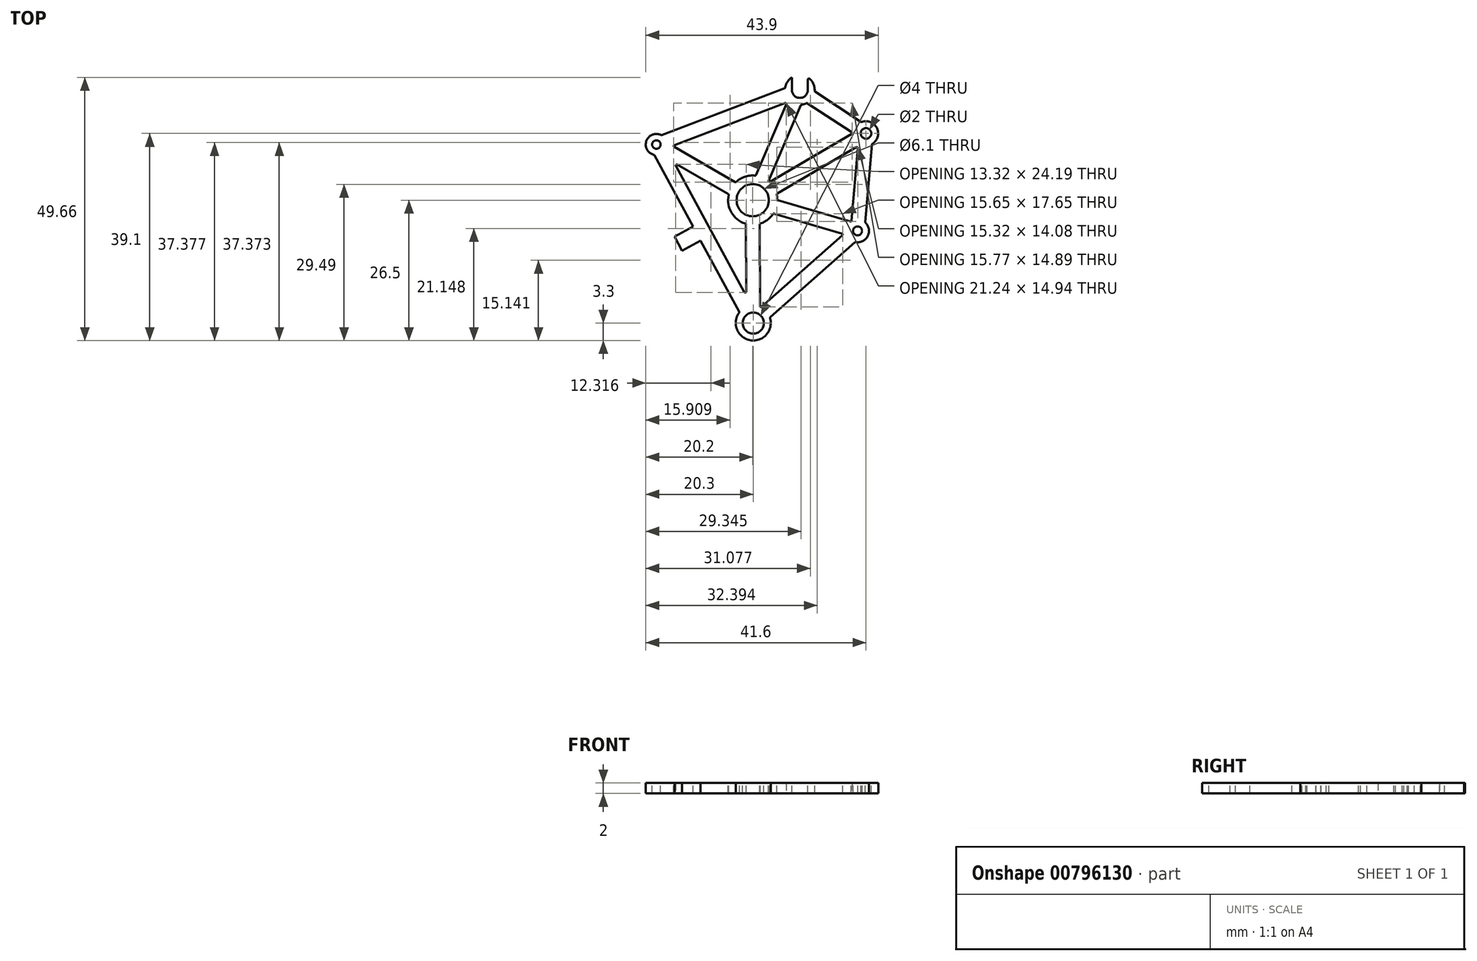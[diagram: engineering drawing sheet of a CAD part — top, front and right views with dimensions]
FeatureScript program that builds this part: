
annotation { "Feature Type Name" : "Feature", "Feature Type Description" : "" }
export const myFeature = defineFeature(function(context is Context, id is Id, definition is map)
    precondition{}
    {
        {
            var Q0;
            Q0=qCreatedBy(makeId("Top.planeOp"),FACE);
            var sketch = newSketch(context, id + "F0", { "sketchPlane" : qUnion([Q0])});
            skCircle(sketch, "E0", {"center": v(4.2, 40) * mm, "radius": 0.8 * mm});
            skCircle(sketch, "E1", {"center": v(31.3, 50.3) * mm, "radius": 1.5 * mm});
            skCircle(sketch, "E2", {"center": v(43.8, 42.1) * mm, "radius": 1 * mm});
            skCircle(sketch, "E3", {"center": v(22.4, 29.5) * mm, "radius": 3.05 * mm});
            skCircle(sketch, "E4", {"center": v(22.5, 6.3) * mm, "radius": 2 * mm});
            skCircle(sketch, "E5", {"center": v(42.2, 23.7) * mm, "radius": 0.85 * mm});
            skSolve(sketch);
        }
        {
            var Q0;
            Q0=qCreatedBy(makeId("Top.planeOp"),FACE);
            var sketch = newSketch(context, id + "F1", { "sketchPlane" : qUnion([Q0])});
            skCircle(sketch, "E6.0", {"center": v(4.2, 40) * mm, "radius": 0.8 * mm});
            skCircle(sketch, "E7.0", {"center": v(22.4, 29.5) * mm, "radius": 3.05 * mm});
            skCircle(sketch, "E8.0", {"center": v(31.3, 50.3) * mm, "radius": 1.5 * mm});
            skCircle(sketch, "E9.0", {"center": v(43.8, 42.1) * mm, "radius": 1 * mm});
            skCircle(sketch, "E10.0", {"center": v(42.2, 23.7) * mm, "radius": 0.85 * mm});
            skCircle(sketch, "E11.0", {"center": v(22.5, 6.3) * mm, "radius": 2 * mm});
            skCircle(sketch, "E12", {"center": v(4.2, 40) * mm, "radius": 2 * mm});
            skCircle(sketch, "E13", {"center": v(31.3, 50.3) * mm, "radius": 2.8 * mm});
            skCircle(sketch, "E14", {"center": v(22.4, 29.5) * mm, "radius": 4.65 * mm});
            skCircle(sketch, "E15", {"center": v(43.8, 42.1) * mm, "radius": 2.3 * mm});
            skCircle(sketch, "E16", {"center": v(42.2, 23.7) * mm, "radius": 2.15 * mm});
            skCircle(sketch, "E17", {"center": v(22.5, 6.3) * mm, "radius": 3.3 * mm});
            skLineSegment(sketch, "E18", {"start": v(5, 40) * mm, "end": v(6.2, 40) * mm, "construction": true});
            skLineSegment(sketch, "E19", {"start": v(24.5, 6.3) * mm, "end": v(25.8, 6.3) * mm, "construction": true});
            skLineSegment(sketch, "E20", {"start": v(4.2, 40) * mm, "end": v(22.5, 6.3) * mm, "construction": true});
            skLineSegment(sketch, "E21", {"start": v(22.5, 6.3) * mm, "end": v(22.4, 29.5) * mm, "construction": true});
            skLineSegment(sketch, "E22", {"start": v(22.4, 29.5) * mm, "end": v(4.2, 40) * mm, "construction": true});
            skLineSegment(sketch, "E23", {"start": v(22.5, 6.3) * mm, "end": v(42.2, 23.7) * mm, "construction": true});
            skLineSegment(sketch, "E24", {"start": v(22.4, 29.5) * mm, "end": v(42.2, 23.7) * mm, "construction": true});
            skLineSegment(sketch, "E25", {"start": v(42.2, 23.7) * mm, "end": v(43.8, 42.1) * mm, "construction": true});
            skLineSegment(sketch, "E26", {"start": v(43.8, 42.1) * mm, "end": v(22.4, 29.5) * mm, "construction": true});
            skLineSegment(sketch, "E27", {"start": v(31.3, 50.3) * mm, "end": v(43.8, 42.1) * mm, "construction": true});
            skLineSegment(sketch, "E28", {"start": v(31.3, 50.3) * mm, "end": v(22.4, 29.5) * mm, "construction": true});
            skLineSegment(sketch, "E29", {"start": v(31.3, 50.3) * mm, "end": v(4.2, 40) * mm, "construction": true});
            skLineSegment(sketch, "E30", {"start": v(29.13, 48.53) * mm, "end": v(22.96, 34.12) * mm});
            skLineSegment(sketch, "E31", {"start": v(26.05, 41.32) * mm, "end": v(28.44, 40.3) * mm, "construction": true});
            skPoint(sketch, "E32", {"position": v(27.24, 40.81) * mm});
            skLineSegment(sketch, "E33", {"start": v(25.35, 33.1) * mm, "end": v(31.52, 47.5) * mm});
            skLineSegment(sketch, "E34", {"start": v(5.16, 41.76) * mm, "end": v(28.52, 50.63) * mm});
            skLineSegment(sketch, "E35", {"start": v(16.84, 46.2) * mm, "end": v(17.76, 43.76) * mm, "construction": true});
            skLineSegment(sketch, "E36", {"start": v(6.08, 39.32) * mm, "end": v(29.44, 48.2) * mm});
            skPoint(sketch, "E37", {"position": v(17.3, 44.98) * mm});
            skLineSegment(sketch, "E38", {"start": v(6.17, 40.37) * mm, "end": v(19.18, 32.86) * mm});
            skLineSegment(sketch, "E39", {"start": v(4.87, 38.11) * mm, "end": v(17.88, 30.6) * mm});
            skLineSegment(sketch, "E40", {"start": v(11.38, 34.36) * mm, "end": v(12.67, 36.61) * mm, "construction": true});
            skPoint(sketch, "E41", {"position": v(12.02, 35.49) * mm});
            skLineSegment(sketch, "E42", {"start": v(23.79, 9.34) * mm, "end": v(23.72, 25.04) * mm});
            skLineSegment(sketch, "E43", {"start": v(21.19, 9.33) * mm, "end": v(21.12, 25.03) * mm});
            skLineSegment(sketch, "E44", {"start": v(21.15, 17.18) * mm, "end": v(23.75, 17.19) * mm, "construction": true});
            skPoint(sketch, "E45", {"position": v(22.45, 17.18) * mm});
            skLineSegment(sketch, "E46", {"start": v(19.91, 8.35) * mm, "end": v(3.78, 38.04) * mm});
            skLineSegment(sketch, "E47", {"start": v(22.2, 9.59) * mm, "end": v(6.07, 39.28) * mm});
            skLineSegment(sketch, "E48", {"start": v(11.85, 23.2) * mm, "end": v(14.13, 24.44) * mm, "construction": true});
            skPoint(sketch, "E49", {"position": v(12.99, 23.81) * mm});
            skLineSegment(sketch, "E50", {"start": v(26.32, 27) * mm, "end": v(40.2, 22.93) * mm});
            skLineSegment(sketch, "E51", {"start": v(33.26, 24.97) * mm, "end": v(33.99, 27.46) * mm, "construction": true});
            skPoint(sketch, "E52", {"position": v(33.62, 26.21) * mm});
            skLineSegment(sketch, "E53", {"start": v(40.92, 25.43) * mm, "end": v(27.05, 29.5) * mm});
            skLineSegment(sketch, "E54", {"start": v(25.63, 7.33) * mm, "end": v(41.78, 21.6) * mm});
            skLineSegment(sketch, "E55", {"start": v(23.91, 9.28) * mm, "end": v(40.06, 23.54) * mm});
            skLineSegment(sketch, "E56", {"start": v(33.7, 14.46) * mm, "end": v(31.98, 16.41) * mm, "construction": true});
            skPoint(sketch, "E57", {"position": v(32.84, 15.44) * mm});
            skLineSegment(sketch, "E58", {"start": v(43.64, 25.3) * mm, "end": v(44.93, 40.1) * mm});
            skLineSegment(sketch, "E59", {"start": v(41.05, 25.52) * mm, "end": v(42.34, 40.32) * mm});
            skLineSegment(sketch, "E60", {"start": v(44.29, 32.7) * mm, "end": v(41.7, 32.92) * mm, "construction": true});
            skPoint(sketch, "E61", {"position": v(43, 32.8) * mm});
            skLineSegment(sketch, "E62", {"start": v(42.93, 44.23) * mm, "end": v(34.09, 50.03) * mm});
            skLineSegment(sketch, "E63", {"start": v(41.5, 42.05) * mm, "end": v(32.66, 47.85) * mm});
            skLineSegment(sketch, "E64", {"start": v(37.08, 44.95) * mm, "end": v(38.5, 47.13) * mm, "construction": true});
            skPoint(sketch, "E65", {"position": v(37.8, 46.04) * mm});
            skLineSegment(sketch, "E66", {"start": v(26.9, 30.64) * mm, "end": v(42.82, 40.02) * mm});
            skLineSegment(sketch, "E67", {"start": v(25.59, 32.89) * mm, "end": v(41.5, 42.26) * mm});
            skLineSegment(sketch, "E68", {"start": v(34.87, 35.33) * mm, "end": v(33.55, 37.57) * mm, "construction": true});
            skPoint(sketch, "E69", {"position": v(34.2, 36.45) * mm});
            skPoint(sketch, "E70", {"position": v(32.55, 49.48) * mm});
            skPoint(sketch, "E71", {"position": v(33.64, 48.76) * mm});
            skPoint(sketch, "E72", {"position": v(41.88, 43.36) * mm});
            skPoint(sketch, "E73", {"position": v(42.96, 42.65) * mm});
            skPoint(sketch, "E74", {"position": v(25.33, 28.64) * mm});
            skPoint(sketch, "E75", {"position": v(26.86, 28.2) * mm});
            skPoint(sketch, "E76", {"position": v(42.27, 24.55) * mm});
            skPoint(sketch, "E77", {"position": v(42.39, 25.84) * mm});
            skLineSegment(sketch, "E78", {"start": v(11.13, 24.51) * mm, "end": v(7.62, 22.6) * mm});
            skLineSegment(sketch, "E79", {"start": v(7.62, 22.6) * mm, "end": v(9.05, 19.97) * mm});
            skLineSegment(sketch, "E80", {"start": v(9.05, 19.97) * mm, "end": v(12.56, 21.88) * mm});
            skLineSegment(sketch, "E81", {"start": v(11.85, 23.2) * mm, "end": v(8.33, 21.29) * mm, "construction": true});
            skSolve(sketch);
        }
        {
            var Q0;
            {var subQ3=sQuery(id+"F1.wireOp",EDGE,"E34");Q0=makeQuery(id+"F1.imprint","IMPRINT",FACE,{"disambiguationData":[TD([[makeQuery(id+"F1.imprint","IMPRINT",EDGE,{"derivedFrom":subQ3}),-1.0]])]});}
            var Q1;
            {var subQ5=sQuery(id+"F1.wireOp",EDGE,"E62");Q1=makeQuery(id+"F1.imprint","IMPRINT",FACE,{"disambiguationData":[TD([[makeQuery(id+"F1.imprint","IMPRINT",EDGE,{"derivedFrom":subQ5}),1.0]])]});}
            var Q2;
            {var subQ0=sQuery(id+"F1.wireOp",EDGE,"E58");Q2=makeQuery(id+"F1.imprint","IMPRINT",FACE,{"disambiguationData":[TD([[makeQuery(id+"F1.imprint","IMPRINT",EDGE,{"derivedFrom":subQ0}),1.0]])]});}
            var Q3;
            {var subQ9=sQuery(id+"F1.wireOp",EDGE,"E54");Q3=makeQuery(id+"F1.imprint","IMPRINT",FACE,{"disambiguationData":[TD([[makeQuery(id+"F1.imprint","IMPRINT",EDGE,{"derivedFrom":subQ9}),1.0]])]});}
            var Q4;
            Q4=makeQuery(id+"F1.imprint","IMPRINT",FACE,{"disambiguationData":[TD([[makeQuery(id+"F1.imprint","IMPRINT",EDGE,{"derivedFrom":sQuery(id+"F1.wireOp",EDGE,"E6.0")}),-1.0]])]});
            var Q5;
            Q5=makeQuery(id+"F1.imprint","IMPRINT",FACE,{"disambiguationData":[TD([[makeQuery(id+"F1.imprint","IMPRINT",EDGE,{"derivedFrom":sQuery(id+"F1.wireOp",EDGE,"E8.0")}),-1.0]])]});
            var Q6;
            Q6=makeQuery(id+"F1.imprint","IMPRINT",FACE,{"disambiguationData":[TD([[makeQuery(id+"F1.imprint","IMPRINT",EDGE,{"derivedFrom":sQuery(id+"F1.wireOp",EDGE,"E9.0")}),-1.0]])]});
            var Q7;
            Q7=makeQuery(id+"F1.imprint","IMPRINT",FACE,{"disambiguationData":[TD([[makeQuery(id+"F1.imprint","IMPRINT",EDGE,{"derivedFrom":sQuery(id+"F1.wireOp",EDGE,"E10.0")}),-1.0]])]});
            var Q8;
            Q8=makeQuery(id+"F1.imprint","IMPRINT",FACE,{"disambiguationData":[TD([[makeQuery(id+"F1.imprint","IMPRINT",EDGE,{"derivedFrom":sQuery(id+"F1.wireOp",EDGE,"E11.0")}),-1.0]])]});
            var Q9;
            {var subQ3=sQuery(id+"F1.wireOp",EDGE,"E36");var subQ6=sQuery(id+"F1.wireOp",EDGE,"E12");var subQ10=makeQuery(id+"F1.imprint","INTERSECT",VERTEX,{"derivedFrom":[subQ6,subQ3]});Q9=makeQuery(id+"F1.imprint","IMPRINT",FACE,{"disambiguationData":[TD([[makeQuery(id+"F1.imprint","IMPRINT",EDGE,{"disambiguationData":[TD([[subQ10,1.0]])],"derivedFrom":subQ6}),-1.0]])]});}
            var Q10;
            {var subQ0=sQuery(id+"F1.wireOp",EDGE,"E36");var subQ1=sQuery(id+"F1.wireOp",EDGE,"E12");var subQ2=makeQuery(id+"F1.imprint","INTERSECT",VERTEX,{"derivedFrom":[subQ1,subQ0]});Q10=makeQuery(id+"F1.imprint","IMPRINT",FACE,{"disambiguationData":[TD([[makeQuery(id+"F1.imprint","IMPRINT",EDGE,{"disambiguationData":[TD([[subQ2,-1.0]])],"derivedFrom":subQ1}),-1.0]])]});}
            var Q11;
            {var subQ0=sQuery(id+"F1.wireOp",EDGE,"E39");var subQ1=sQuery(id+"F1.wireOp",EDGE,"E12");var subQ2=makeQuery(id+"F1.imprint","INTERSECT",VERTEX,{"derivedFrom":[subQ1,subQ0]});Q11=makeQuery(id+"F1.imprint","IMPRINT",FACE,{"disambiguationData":[TD([[makeQuery(id+"F1.imprint","IMPRINT",EDGE,{"disambiguationData":[TD([[subQ2,-1.0]])],"derivedFrom":subQ1}),-1.0]])]});}
            var Q12;
            {var subQ9=sQuery(id+"F1.wireOp",EDGE,"E46");Q12=makeQuery(id+"F1.imprint","IMPRINT",FACE,{"disambiguationData":[TD([[makeQuery(id+"F1.imprint","IMPRINT",EDGE,{"derivedFrom":subQ9}),-1.0]])]});}
            var Q13;
            {var subQ0=sQuery(id+"F1.wireOp",EDGE,"E43");var subQ1=sQuery(id+"F1.wireOp",EDGE,"E17");var subQ2=makeQuery(id+"F1.imprint","INTERSECT",VERTEX,{"derivedFrom":[subQ1,subQ0]});Q13=makeQuery(id+"F1.imprint","IMPRINT",FACE,{"disambiguationData":[TD([[makeQuery(id+"F1.imprint","IMPRINT",EDGE,{"disambiguationData":[TD([[subQ2,1.0]])],"derivedFrom":subQ1}),-1.0]])]});}
            var Q14;
            {var subQ0=sQuery(id+"F1.wireOp",EDGE,"E42");var subQ1=sQuery(id+"F1.wireOp",EDGE,"E17");var subQ2=makeQuery(id+"F1.imprint","INTERSECT",VERTEX,{"derivedFrom":[subQ1,subQ0]});Q14=makeQuery(id+"F1.imprint","IMPRINT",FACE,{"disambiguationData":[TD([[makeQuery(id+"F1.imprint","IMPRINT",EDGE,{"disambiguationData":[TD([[subQ2,-1.0]])],"derivedFrom":subQ1}),-1.0]])]});}
            var Q15;
            {var subQ0=sQuery(id+"F1.wireOp",EDGE,"E43");var subQ1=sQuery(id+"F1.wireOp",EDGE,"E14");var subQ2=makeQuery(id+"F1.imprint","INTERSECT",VERTEX,{"derivedFrom":[subQ1,subQ0]});Q15=makeQuery(id+"F1.imprint","IMPRINT",FACE,{"disambiguationData":[TD([[makeQuery(id+"F1.imprint","IMPRINT",EDGE,{"disambiguationData":[TD([[subQ2,-1.0]])],"derivedFrom":subQ1}),-1.0]])]});}
            var Q16;
            {var subQ0=sQuery(id+"F1.wireOp",EDGE,"E50");var subQ1=sQuery(id+"F1.wireOp",EDGE,"E16");var subQ2=makeQuery(id+"F1.imprint","INTERSECT",VERTEX,{"derivedFrom":[subQ1,subQ0]});Q16=makeQuery(id+"F1.imprint","IMPRINT",FACE,{"disambiguationData":[TD([[makeQuery(id+"F1.imprint","IMPRINT",EDGE,{"disambiguationData":[TD([[subQ2,1.0]])],"derivedFrom":subQ1}),-1.0]])]});}
            var Q17;
            {var subQ0=sQuery(id+"F1.wireOp",EDGE,"E53");var subQ1=sQuery(id+"F1.wireOp",EDGE,"E16");var subQ2=makeQuery(id+"F1.imprint","INTERSECT",VERTEX,{"derivedFrom":[subQ1,subQ0]});Q17=makeQuery(id+"F1.imprint","IMPRINT",FACE,{"disambiguationData":[TD([[makeQuery(id+"F1.imprint","IMPRINT",EDGE,{"disambiguationData":[TD([[subQ2,-1.0]])],"derivedFrom":subQ1}),-1.0]])]});}
            var Q18;
            {var subQ0=sQuery(id+"F1.wireOp",EDGE,"E30");var subQ1=sQuery(id+"F1.wireOp",EDGE,"E13");var subQ2=makeQuery(id+"F1.imprint","INTERSECT",VERTEX,{"derivedFrom":[subQ1,subQ0]});Q18=makeQuery(id+"F1.imprint","IMPRINT",FACE,{"disambiguationData":[TD([[makeQuery(id+"F1.imprint","IMPRINT",EDGE,{"disambiguationData":[TD([[subQ2,-1.0]])],"derivedFrom":subQ1}),-1.0]])]});}
            var Q19;
            {var subQ0=sQuery(id+"F1.wireOp",EDGE,"E33");var subQ1=sQuery(id+"F1.wireOp",EDGE,"E13");var subQ2=makeQuery(id+"F1.imprint","INTERSECT",VERTEX,{"derivedFrom":[subQ1,subQ0]});Q19=makeQuery(id+"F1.imprint","IMPRINT",FACE,{"disambiguationData":[TD([[makeQuery(id+"F1.imprint","IMPRINT",EDGE,{"disambiguationData":[TD([[subQ2,1.0]])],"derivedFrom":subQ1}),-1.0]])]});}
            var Q20;
            {var subQ0=sQuery(id+"F1.wireOp",EDGE,"E42");var subQ1=sQuery(id+"F1.wireOp",EDGE,"E14");var subQ2=makeQuery(id+"F1.imprint","INTERSECT",VERTEX,{"derivedFrom":[subQ1,subQ0]});Q20=makeQuery(id+"F1.imprint","IMPRINT",FACE,{"disambiguationData":[TD([[makeQuery(id+"F1.imprint","IMPRINT",EDGE,{"disambiguationData":[TD([[subQ2,1.0]])],"derivedFrom":subQ1}),-1.0]])]});}
            var Q21;
            {var subQ8=sQuery(id+"F1.wireOp",EDGE,"E36");var subQ11=sQuery(id+"F1.wireOp",EDGE,"E13");var subQ12=makeQuery(id+"F1.imprint","INTERSECT",VERTEX,{"derivedFrom":[subQ11,subQ8]});Q21=makeQuery(id+"F1.imprint","IMPRINT",FACE,{"disambiguationData":[TD([[makeQuery(id+"F1.imprint","IMPRINT",EDGE,{"disambiguationData":[TD([[subQ12,-1.0]])],"derivedFrom":subQ11}),-1.0]])]});}
            var Q22;
            {var subQ0=sQuery(id+"F1.wireOp",EDGE,"E33");var subQ1=sQuery(id+"F1.wireOp",EDGE,"E14");var subQ2=makeQuery(id+"F1.imprint","INTERSECT",VERTEX,{"derivedFrom":[subQ1,subQ0]});Q22=makeQuery(id+"F1.imprint","IMPRINT",FACE,{"disambiguationData":[TD([[makeQuery(id+"F1.imprint","IMPRINT",EDGE,{"disambiguationData":[TD([[subQ2,-1.0]])],"derivedFrom":subQ1}),-1.0]])]});}
            var Q23;
            Q23=makeQuery(id+"F1.imprint","IMPRINT",FACE,{"disambiguationData":[TD([[makeQuery(id+"F1.imprint","IMPRINT",EDGE,{"derivedFrom":sQuery(id+"F1.wireOp",EDGE,"E7.0")}),-1.0]])]});
            var Q24;
            {var subQ0=sQuery(id+"F1.wireOp",EDGE,"E53");var subQ1=sQuery(id+"F1.wireOp",EDGE,"E14");var subQ2=makeQuery(id+"F1.imprint","INTERSECT",VERTEX,{"derivedFrom":[subQ1,subQ0]});Q24=makeQuery(id+"F1.imprint","IMPRINT",FACE,{"disambiguationData":[TD([[makeQuery(id+"F1.imprint","IMPRINT",EDGE,{"disambiguationData":[TD([[subQ2,1.0]])],"derivedFrom":subQ1}),-1.0]])]});}
            var Q25;
            {var subQ0=sQuery(id+"F1.wireOp",EDGE,"E63");var subQ1=sQuery(id+"F1.wireOp",EDGE,"E15");var subQ2=makeQuery(id+"F1.imprint","INTERSECT",VERTEX,{"derivedFrom":[subQ1,subQ0]});Q25=makeQuery(id+"F1.imprint","IMPRINT",FACE,{"disambiguationData":[TD([[makeQuery(id+"F1.imprint","IMPRINT",EDGE,{"disambiguationData":[TD([[subQ2,1.0]])],"derivedFrom":subQ1}),-1.0]])]});}
            var Q26;
            {var subQ0=sQuery(id+"F1.wireOp",EDGE,"E59");var subQ1=sQuery(id+"F1.wireOp",EDGE,"E15");var subQ2=makeQuery(id+"F1.imprint","INTERSECT",VERTEX,{"derivedFrom":[subQ1,subQ0]});Q26=makeQuery(id+"F1.imprint","IMPRINT",FACE,{"disambiguationData":[TD([[makeQuery(id+"F1.imprint","IMPRINT",EDGE,{"disambiguationData":[TD([[subQ2,-1.0]])],"derivedFrom":subQ1}),-1.0]])]});}
            var Q27;
            {var subQ7=sQuery(id+"F1.wireOp",EDGE,"E66");var subQ9=sQuery(id+"F1.wireOp",EDGE,"E14");var subQ10=makeQuery(id+"F1.imprint","INTERSECT",VERTEX,{"derivedFrom":[subQ9,subQ7]});Q27=makeQuery(id+"F1.imprint","IMPRINT",FACE,{"disambiguationData":[TD([[makeQuery(id+"F1.imprint","IMPRINT",EDGE,{"disambiguationData":[TD([[subQ10,-1.0]])],"derivedFrom":subQ9}),-1.0]])]});}
            var Q28;
            {var subQ0=sQuery(id+"F1.wireOp",EDGE,"E78");Q28=makeQuery(id+"F1.imprint","IMPRINT",FACE,{"disambiguationData":[TD([[makeQuery(id+"F1.imprint","IMPRINT",EDGE,{"derivedFrom":subQ0}),1.0]])]});}
            extrude(context, id + "F2", {"entities" : qUnion([Q0, Q1, Q2, Q3, Q4, Q5, Q6, Q7, Q8, Q9, Q10, Q11, Q12, Q13, Q14, Q15, Q16, Q17, Q18, Q19, Q20, Q21, Q22, Q23, Q24, Q25, Q26, Q27, Q28]), "oppositeDirection" : true, "depth" : 2 * mm, "offsetDistance" : 25 * mm});
        }
        {
            var Q0;
            Q0=makeQuery(id+"F2.opExtrude","CAP_FACE",FACE,{"disambiguationData":[OSD([sQuery(id+"F1.wireOp",EDGE,"E6.0"),sQuery(id+"F1.wireOp",EDGE,"E7.0"),sQuery(id+"F1.wireOp",EDGE,"E8.0"),sQuery(id+"F1.wireOp",EDGE,"E9.0"),sQuery(id+"F1.wireOp",EDGE,"E10.0"),sQuery(id+"F1.wireOp",EDGE,"E11.0"),sQuery(id+"F1.wireOp",EDGE,"E12"),sQuery(id+"F1.wireOp",EDGE,"E13"),sQuery(id+"F1.wireOp",EDGE,"E14"),sQuery(id+"F1.wireOp",EDGE,"E15"),sQuery(id+"F1.wireOp",EDGE,"E16"),sQuery(id+"F1.wireOp",EDGE,"E17"),sQuery(id+"F1.wireOp",EDGE,"E30"),sQuery(id+"F1.wireOp",EDGE,"E33"),sQuery(id+"F1.wireOp",EDGE,"E34"),sQuery(id+"F1.wireOp",EDGE,"E36"),sQuery(id+"F1.wireOp",EDGE,"E38"),sQuery(id+"F1.wireOp",EDGE,"E39"),sQuery(id+"F1.wireOp",EDGE,"E42"),sQuery(id+"F1.wireOp",EDGE,"E43"),sQuery(id+"F1.wireOp",EDGE,"E46"),sQuery(id+"F1.wireOp",EDGE,"E47"),sQuery(id+"F1.wireOp",EDGE,"E50"),sQuery(id+"F1.wireOp",EDGE,"E53"),sQuery(id+"F1.wireOp",EDGE,"E54"),sQuery(id+"F1.wireOp",EDGE,"E55"),sQuery(id+"F1.wireOp",EDGE,"E58"),sQuery(id+"F1.wireOp",EDGE,"E59"),sQuery(id+"F1.wireOp",EDGE,"E62"),sQuery(id+"F1.wireOp",EDGE,"E63")])],"isStart":true});
            var sketch = newSketch(context, id + "F3", { "sketchPlane" : qUnion([Q0])});
            skLineSegment(sketch, "E82", {"start": v(29.8, 50.3) * mm, "end": v(29.8, 52.66) * mm});
            skLineSegment(sketch, "E83", {"start": v(32.8, 50.3) * mm, "end": v(32.8, 52.66) * mm});
            skSolve(sketch);
        }
        {
            var Q0;
            {var subQ0=sQuery(id+"F3.wireOp",EDGE,"E82");Q0=makeQuery(id+"F3.imprint","IMPRINT",FACE,{"disambiguationData":[TD([[makeQuery(id+"F3.imprint","IMPRINT",EDGE,{"derivedFrom":subQ0}),-1.0]])]});}
            extrude(context, id + "F4", {"entities" : qUnion([Q0]), "operationType" : NewBodyOperationType.REMOVE, "endBound" : BoundingType.THROUGH_ALL, "oppositeDirection" : true, "depth" : 25 * mm, "offsetDistance" : 25 * mm});
        }
        {
            var Q0;
            Q0=makeQuery(id+"F2.opExtrude","SWEPT_EDGE",EDGE,{"disambiguationData":[OSD([sQuery(id+"F1.wireOp",EDGE,"E36"),sQuery(id+"F1.wireOp",EDGE,"E38")])]});
            var Q1;
            Q1=makeQuery(id+"F2.opExtrude","SWEPT_EDGE",EDGE,{"disambiguationData":[OSD([sQuery(id+"F1.wireOp",EDGE,"E39"),sQuery(id+"F1.wireOp",EDGE,"E47")])]});
            var Q2;
            Q2=makeQuery(id+"F2.opExtrude","SWEPT_EDGE",EDGE,{"disambiguationData":[OSD([sQuery(id+"F1.wireOp",EDGE,"E43"),sQuery(id+"F1.wireOp",EDGE,"E47")])]});
            var Q3;
            Q3=makeQuery(id+"F2.opExtrude","SWEPT_EDGE",EDGE,{"disambiguationData":[OSD([sQuery(id+"F1.wireOp",EDGE,"E42"),sQuery(id+"F1.wireOp",EDGE,"E55")])]});
            var Q4;
            Q4=makeQuery(id+"F2.opExtrude","SWEPT_EDGE",EDGE,{"disambiguationData":[OSD([sQuery(id+"F1.wireOp",EDGE,"E17"),sQuery(id+"F1.wireOp",EDGE,"E46")])]});
            var Q5;
            Q5=makeQuery(id+"F2.opExtrude","SWEPT_EDGE",EDGE,{"disambiguationData":[OSD([sQuery(id+"F1.wireOp",EDGE,"E17"),sQuery(id+"F1.wireOp",EDGE,"E54")])]});
            var Q6;
            Q6=makeQuery(id+"F2.opExtrude","SWEPT_EDGE",EDGE,{"disambiguationData":[OSD([sQuery(id+"F1.wireOp",EDGE,"E14"),sQuery(id+"F1.wireOp",EDGE,"E43")])]});
            var Q7;
            Q7=makeQuery(id+"F2.opExtrude","SWEPT_EDGE",EDGE,{"disambiguationData":[OSD([sQuery(id+"F1.wireOp",EDGE,"E14"),sQuery(id+"F1.wireOp",EDGE,"E39")])]});
            var Q8;
            Q8=makeQuery(id+"F2.opExtrude","SWEPT_EDGE",EDGE,{"disambiguationData":[OSD([sQuery(id+"F1.wireOp",EDGE,"E12"),sQuery(id+"F1.wireOp",EDGE,"E46")])]});
            var Q9;
            Q9=makeQuery(id+"F2.opExtrude","SWEPT_EDGE",EDGE,{"disambiguationData":[OSD([sQuery(id+"F1.wireOp",EDGE,"E12"),sQuery(id+"F1.wireOp",EDGE,"E34")])]});
            var Q10;
            Q10=makeQuery(id+"F2.opExtrude","SWEPT_EDGE",EDGE,{"disambiguationData":[OSD([sQuery(id+"F1.wireOp",EDGE,"E13"),sQuery(id+"F1.wireOp",EDGE,"E34")])]});
            var Q11;
            Q11=makeQuery(id+"F2.opExtrude","SWEPT_EDGE",EDGE,{"disambiguationData":[OSD([sQuery(id+"F1.wireOp",EDGE,"E30"),sQuery(id+"F1.wireOp",EDGE,"E36")])]});
            var Q12;
            Q12=makeQuery(id+"F2.opExtrude","SWEPT_EDGE",EDGE,{"disambiguationData":[OSD([sQuery(id+"F1.wireOp",EDGE,"E33"),sQuery(id+"F1.wireOp",EDGE,"E63")])]});
            var Q13;
            Q13=makeQuery(id+"F2.opExtrude","SWEPT_EDGE",EDGE,{"disambiguationData":[OSD([sQuery(id+"F1.wireOp",EDGE,"E13"),sQuery(id+"F1.wireOp",EDGE,"E62")])]});
            var Q14;
            Q14=makeQuery(id+"F2.opExtrude","SWEPT_EDGE",EDGE,{"disambiguationData":[OSD([sQuery(id+"F1.wireOp",EDGE,"E15"),sQuery(id+"F1.wireOp",EDGE,"E62")])]});
            var Q15;
            Q15=makeQuery(id+"F2.opExtrude","SWEPT_EDGE",EDGE,{"disambiguationData":[OSD([sQuery(id+"F1.wireOp",EDGE,"E15"),sQuery(id+"F1.wireOp",EDGE,"E58")])]});
            var Q16;
            Q16=makeQuery(id+"F2.opExtrude","SWEPT_EDGE",EDGE,{"disambiguationData":[OSD([sQuery(id+"F1.wireOp",EDGE,"E59"),sQuery(id+"F1.wireOp",EDGE,"E66")])]});
            var Q17;
            Q17=makeQuery(id+"F2.opExtrude","SWEPT_EDGE",EDGE,{"disambiguationData":[OSD([sQuery(id+"F1.wireOp",EDGE,"E63"),sQuery(id+"F1.wireOp",EDGE,"E67")])]});
            var Q18;
            Q18=makeQuery(id+"F2.opExtrude","SWEPT_EDGE",EDGE,{"disambiguationData":[OSD([sQuery(id+"F1.wireOp",EDGE,"E16"),sQuery(id+"F1.wireOp",EDGE,"E58")])]});
            var Q19;
            Q19=makeQuery(id+"F2.opExtrude","SWEPT_EDGE",EDGE,{"disambiguationData":[OSD([sQuery(id+"F1.wireOp",EDGE,"E16"),sQuery(id+"F1.wireOp",EDGE,"E54")])]});
            var Q20;
            Q20=makeQuery(id+"F2.opExtrude","SWEPT_EDGE",EDGE,{"disambiguationData":[OSD([sQuery(id+"F1.wireOp",EDGE,"E50"),sQuery(id+"F1.wireOp",EDGE,"E55")])]});
            var Q21;
            Q21=makeQuery(id+"F2.opExtrude","SWEPT_EDGE",EDGE,{"disambiguationData":[OSD([sQuery(id+"F1.wireOp",EDGE,"E53"),sQuery(id+"F1.wireOp",EDGE,"E59")])]});
            var Q22;
            Q22=makeQuery(id+"F2.opExtrude","SWEPT_EDGE",EDGE,{"disambiguationData":[OSD([sQuery(id+"F1.wireOp",EDGE,"E14"),sQuery(id+"F1.wireOp",EDGE,"E30")])]});
            var Q23;
            Q23=makeQuery(id+"F2.opExtrude","SWEPT_EDGE",EDGE,{"disambiguationData":[OSD([sQuery(id+"F1.wireOp",EDGE,"E33"),sQuery(id+"F1.wireOp",EDGE,"E67")])]});
            var Q24;
            Q24=makeQuery(id+"F2.opExtrude","SWEPT_EDGE",EDGE,{"disambiguationData":[OSD([sQuery(id+"F1.wireOp",EDGE,"E53"),sQuery(id+"F1.wireOp",EDGE,"E66")])]});
            var Q25;
            Q25=makeQuery(id+"F2.opExtrude","SWEPT_EDGE",EDGE,{"disambiguationData":[OSD([sQuery(id+"F1.wireOp",EDGE,"E42"),sQuery(id+"F1.wireOp",EDGE,"E50")])]});
            var Q26;
            Q26=makeQuery(id+"F2.opExtrude","SWEPT_EDGE",EDGE,{"disambiguationData":[OSD([sQuery(id+"F1.wireOp",EDGE,"E14"),sQuery(id+"F1.wireOp",EDGE,"E38")])]});
            var Q27;
            Q27=makeQuery(id+"F4.boolean.opBoolean","COPY",EDGE,{"derivedFrom":makeQuery(id+"F4.opExtrude","SWEPT_EDGE",EDGE,{"disambiguationData":[OSD([sQuery(id+"F1.wireOp",EDGE,"E13"),sQuery(id+"F3.wireOp",EDGE,"E82")])]})});
            var Q28;
            Q28=makeQuery(id+"F4.boolean.opBoolean","COPY",EDGE,{"derivedFrom":makeQuery(id+"F4.opExtrude","SWEPT_EDGE",EDGE,{"disambiguationData":[OSD([sQuery(id+"F1.wireOp",EDGE,"E13"),sQuery(id+"F3.wireOp",EDGE,"E83")])]})});
            fillet(context, id + "F5", {"entities" : qUnion([Q0, Q1, Q2, Q3, Q4, Q5, Q6, Q7, Q8, Q9, Q10, Q11, Q12, Q13, Q14, Q15, Q16, Q17, Q18, Q19, Q20, Q21, Q22, Q23, Q24, Q25, Q26, Q27, Q28]), "radius" : 0.2 * mm, "tangentPropagation" : true, "allowEdgeOverflow" : false});
        }
    });
